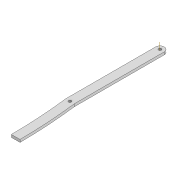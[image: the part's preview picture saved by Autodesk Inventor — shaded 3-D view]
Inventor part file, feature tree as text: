
AUTODESK INVENTOR PART (.ipt)
format: ipt  version: 2022 (Build 260153000, 153)  size: 109,568 bytes
history: native  units: mm
features: extrude x2, sketch x2, other x1
ambient origin geometry x8: Origin, YZ Plane, XZ Plane, XY Plane, X Axis, Y Axis, Z Axis, Center Point
bodies: Solid1 (feature_tree)
feature tree (5):
  extrude  "Extrusion1"  Depth=3.3mm
  other  "Work Axis3"
  extrude  "Extrusion2"  Depth=322.934mm
  sketch  "Sketch1"  dims[d0=3.3mm d1=3.3mm]
  sketch  "Sketch2"  dims[d2=10.0mm d3=322.934mm d4=3.3mm d5=74.182mm d6=3.0mm d7=0.0mm d8=3.3mm d9=218.733mm d12=600.0mm d13=600.0mm d14=100.0mm d15=0.0mm]
